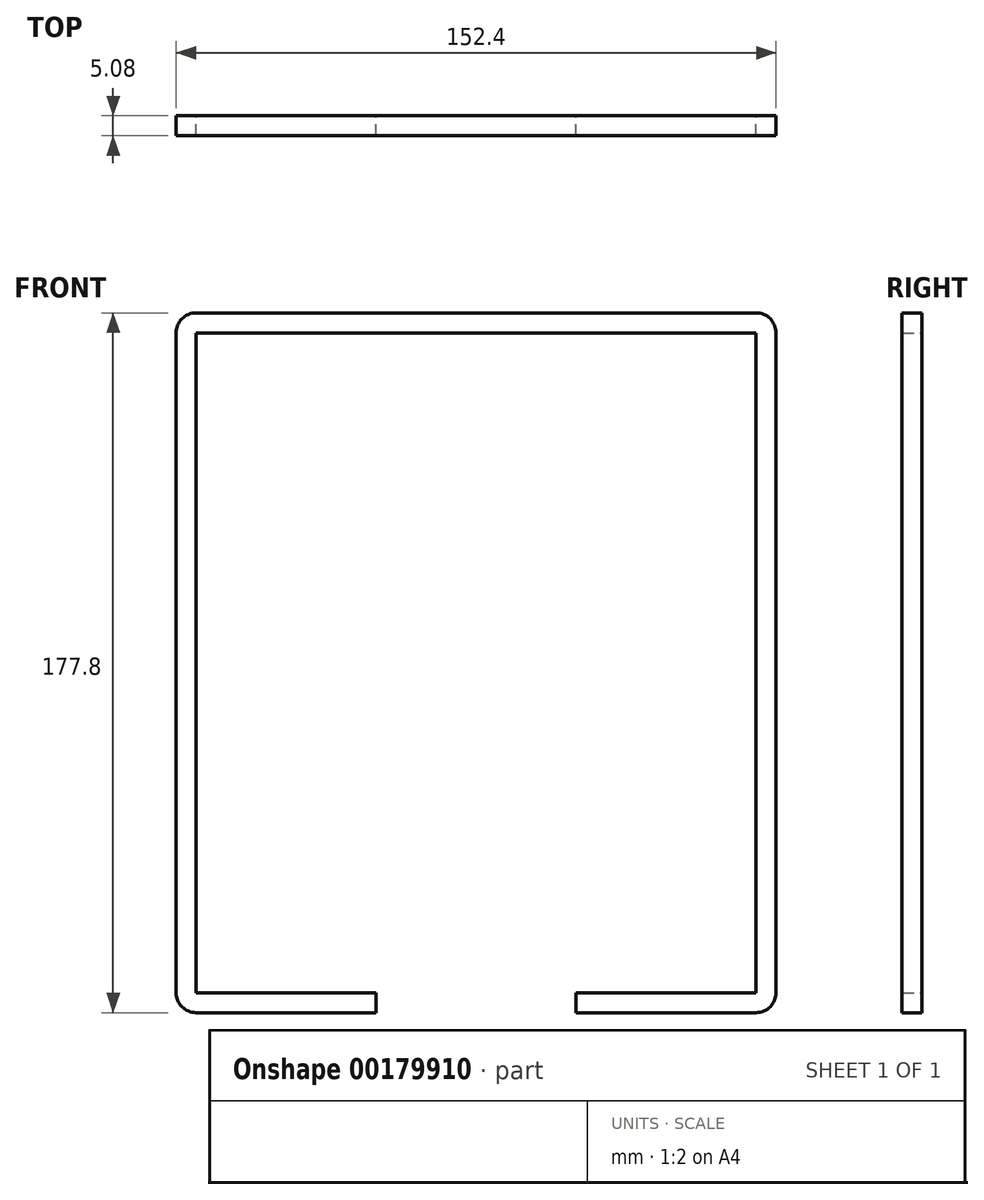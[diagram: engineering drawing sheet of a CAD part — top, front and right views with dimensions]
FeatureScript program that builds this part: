
annotation { "Feature Type Name" : "Feature", "Feature Type Description" : "" }
export const myFeature = defineFeature(function(context is Context, id is Id, definition is map)
    precondition{}
    {
        {
            var Q0;
            Q0=qCreatedBy(makeId("Front.planeOp"),FACE);
            var sketch = newSketch(context, id + "F0", { "sketchPlane" : qUnion([Q0])});
            skLineSegment(sketch, "E0", {"start": v(-101.6, -81.85) * mm, "end": v(-101.6, 95.95) * mm});
            skLineSegment(sketch, "E1", {"start": v(-101.6, 95.95) * mm, "end": v(50.8, 95.95) * mm});
            skLineSegment(sketch, "E2", {"start": v(50.8, 95.95) * mm, "end": v(50.8, -81.85) * mm});
            skLineSegment(sketch, "E3", {"start": v(-101.6, -81.85) * mm, "end": v(-50.8, -81.85) * mm});
            skLineSegment(sketch, "E4", {"start": v(50.8, -81.85) * mm, "end": v(0, -81.85) * mm});
            skLineSegment(sketch, "E5", {"start": v(-50.8, -81.85) * mm, "end": v(-50.8, -76.77) * mm});
            skLineSegment(sketch, "E6", {"start": v(-50.8, -76.77) * mm, "end": v(-96.52, -76.77) * mm});
            skLineSegment(sketch, "E7", {"start": v(-96.52, -76.77) * mm, "end": v(-96.52, 90.87) * mm});
            skLineSegment(sketch, "E8", {"start": v(-96.52, 90.87) * mm, "end": v(45.72, 90.87) * mm});
            skLineSegment(sketch, "E9", {"start": v(45.72, 90.87) * mm, "end": v(45.72, -76.77) * mm});
            skLineSegment(sketch, "E10", {"start": v(45.72, -76.77) * mm, "end": v(0, -76.77) * mm});
            skLineSegment(sketch, "E11", {"start": v(0, -76.77) * mm, "end": v(0, -81.85) * mm});
            skSolve(sketch);
        }
        {
            var Q0;
            Q0 = qSketchRegion(id + "F0", true);
            extrude(context, id + "F1", {"entities" : qUnion([Q0]), "depth" : 5.08 * mm});
        }
        {
            var Q0;
            Q0=makeQuery(id+"F1.opExtrude","SWEPT_EDGE",EDGE,{"disambiguationData":[OSD([sQuery(id+"F0.wireOp",EDGE,"E0"),sQuery(id+"F0.wireOp",EDGE,"E1")])]});
            fillet(context, id + "F2", {"entities" : qUnion([Q0]), "radius" : 5.08 * mm, "tangentPropagation" : true, "allowEdgeOverflow" : false});
        }
        {
            var Q0;
            Q0=makeQuery(id+"F1.opExtrude","SWEPT_EDGE",EDGE,{"disambiguationData":[OSD([sQuery(id+"F0.wireOp",EDGE,"E1"),sQuery(id+"F0.wireOp",EDGE,"E2")])]});
            fillet(context, id + "F3", {"entities" : qUnion([Q0]), "radius" : 5.08 * mm, "tangentPropagation" : true, "allowEdgeOverflow" : false});
        }
        {
            var Q0;
            Q0=makeQuery(id+"F1.opExtrude","SWEPT_EDGE",EDGE,{"disambiguationData":[OSD([sQuery(id+"F0.wireOp",EDGE,"E0"),sQuery(id+"F0.wireOp",EDGE,"E3")])]});
            fillet(context, id + "F4", {"entities" : qUnion([Q0]), "radius" : 5.08 * mm, "tangentPropagation" : true, "allowEdgeOverflow" : false});
        }
        {
            var Q0;
            Q0=makeQuery(id+"F1.opExtrude","SWEPT_EDGE",EDGE,{"disambiguationData":[OSD([sQuery(id+"F0.wireOp",EDGE,"E2"),sQuery(id+"F0.wireOp",EDGE,"E4")])]});
            fillet(context, id + "F5", {"entities" : qUnion([Q0]), "radius" : 5.08 * mm, "tangentPropagation" : true, "allowEdgeOverflow" : false});
        }
    });
